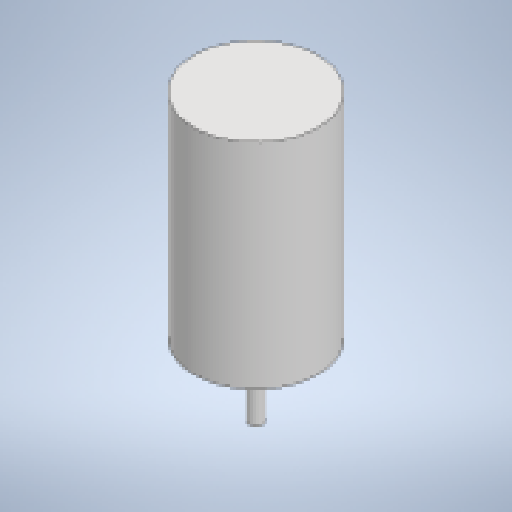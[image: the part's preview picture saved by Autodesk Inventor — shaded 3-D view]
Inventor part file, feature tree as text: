
AUTODESK INVENTOR PART (.ipt)
format: ipt  version: 2023 (Build 270158000, 158)  size: 135,168 bytes
history: native  units: in
note: dims shown in document units (in); Inventor stores cm internally (conversion verified against a paired STEP export)
features: revolve x1, sketch x1
ambient origin geometry x8: Origin, YZ Plane, XZ Plane, XY Plane, X Axis, Y Axis, Z Axis, Center Point
bodies: Solid1 (feature_tree)
feature tree (2):
  revolve  "Revolution1"  [1 undecoded]
  sketch  "Sketch1"  dims[d0=1.75in d1=6.0in d2=360.0deg d3=0.1875in d4=2.0in]
note: 1 required parameter value undecoded (feature->parameter linkage not recoverable at this tier; creation-order binding heuristic only, values carry confidence <= 0.55)
